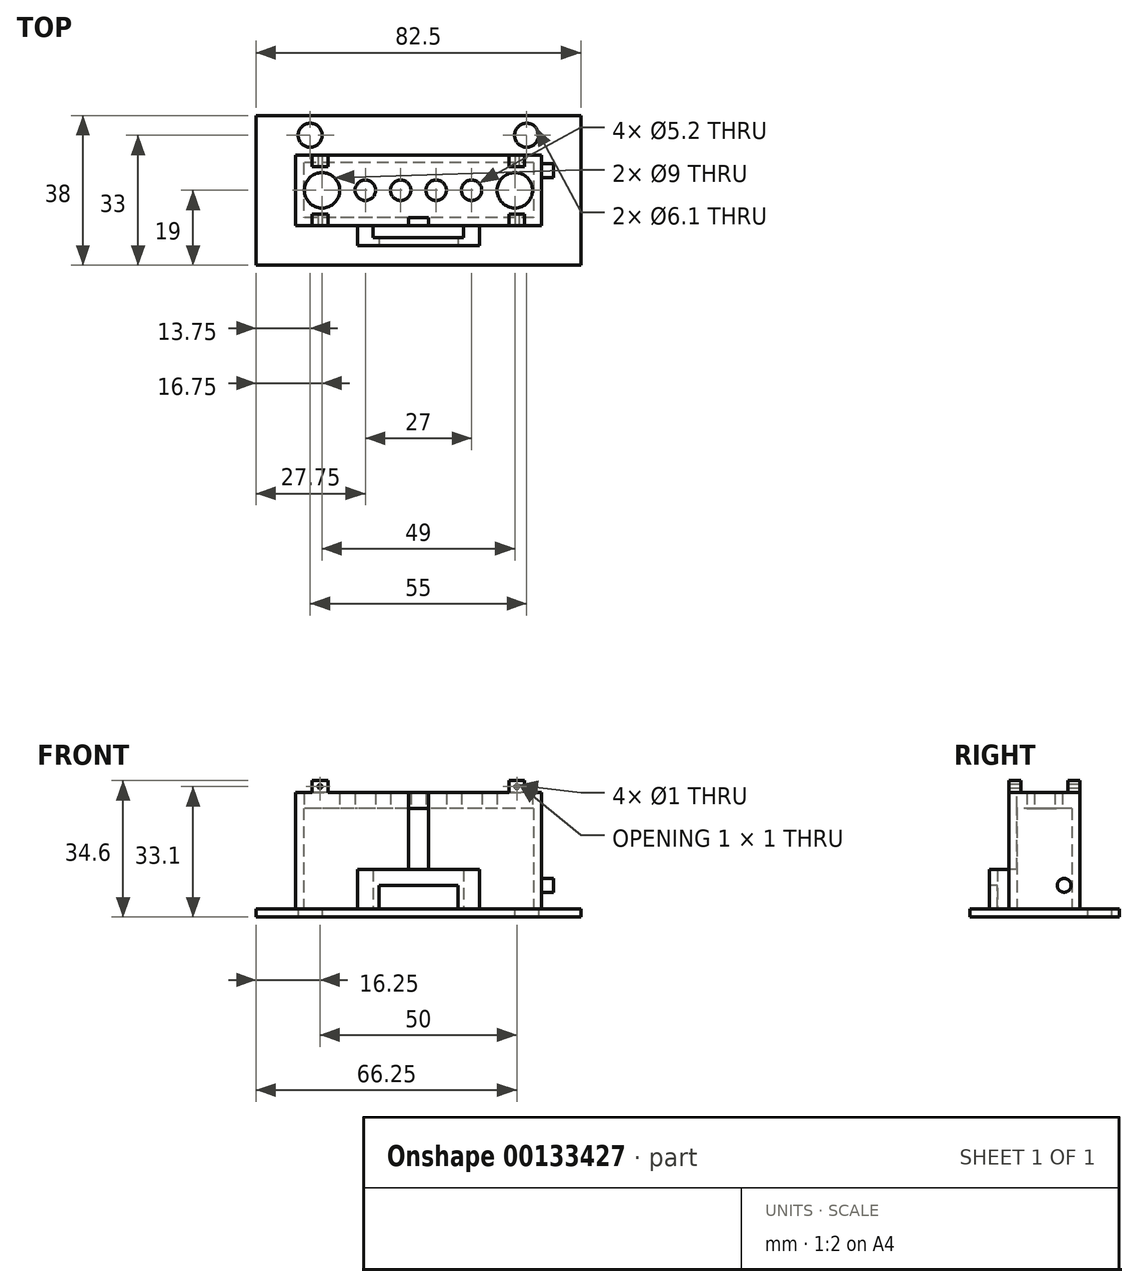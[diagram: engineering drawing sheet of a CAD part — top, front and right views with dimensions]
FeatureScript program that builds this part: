
annotation { "Feature Type Name" : "Feature", "Feature Type Description" : "" }
export const myFeature = defineFeature(function(context is Context, id is Id, definition is map)
    precondition{}
    {
        {
            var Q0;
            Q0=qCreatedBy(makeId("Top.planeOp"),FACE);
            var sketch = newSketch(context, id + "F0", { "sketchPlane" : qUnion([Q0])});
            skLineSegment(sketch, "E0.bottom", {"start": v(31.25, 9) * mm, "end": v(-31.25, 9) * mm});
            skLineSegment(sketch, "E0.top", {"start": v(31.25, -9) * mm, "end": v(-31.25, -9) * mm});
            skLineSegment(sketch, "E0.left", {"start": v(31.25, 9) * mm, "end": v(31.25, -9) * mm});
            skLineSegment(sketch, "E0.right", {"start": v(-31.25, 9) * mm, "end": v(-31.25, -9) * mm});
            skPoint(sketch, "E0.middle", {"position": v(0, 0) * mm});
            skLineSegment(sketch, "E1", {"start": v(-31.25, -9) * mm, "end": v(-31.25, 0) * mm});
            skLineSegment(sketch, "E2", {"start": v(-31.25, 0) * mm, "end": v(31.25, 0) * mm});
            skLineSegment(sketch, "E3", {"start": v(-13.5, 0) * mm, "end": v(-4.5, 0) * mm, "construction": true});
            skCircle(sketch, "E4", {"center": v(-4.5, 0) * mm, "radius": 2.6 * mm});
            skCircle(sketch, "E5.MirrorC", {"center": v(4.5, 0) * mm, "radius": 2.6 * mm});
            skLineSegment(sketch, "E6.0", {"start": v(29.25, -7) * mm, "end": v(-29.25, -7) * mm});
            skLineSegment(sketch, "E6.1", {"start": v(29.25, 7) * mm, "end": v(29.25, -7) * mm});
            skLineSegment(sketch, "E6.2", {"start": v(29.25, 7) * mm, "end": v(-29.25, 7) * mm});
            skLineSegment(sketch, "E6.3", {"start": v(-29.25, 7) * mm, "end": v(-29.25, -7) * mm});
            skCircle(sketch, "E7", {"center": v(-13.5, 0) * mm, "radius": 2.6 * mm});
            skLineSegment(sketch, "E8", {"start": v(4.5, 0) * mm, "end": v(4.5, 0) * mm});
            skCircle(sketch, "E9.MirrorC", {"center": v(13.5, 0) * mm, "radius": 2.6 * mm});
            skLineSegment(sketch, "E10.0", {"start": v(41.25, 19) * mm, "end": v(-41.25, 19) * mm});
            skLineSegment(sketch, "E10.1", {"start": v(41.25, 19) * mm, "end": v(41.25, -19) * mm});
            skLineSegment(sketch, "E10.2", {"start": v(41.25, -19) * mm, "end": v(-41.25, -19) * mm});
            skLineSegment(sketch, "E10.3", {"start": v(-41.25, 19) * mm, "end": v(-41.25, -19) * mm});
            skLineSegment(sketch, "E11", {"start": v(-41.25, 19) * mm, "end": v(-41.25, 14) * mm});
            skLineSegment(sketch, "E12", {"start": v(-41.25, 14) * mm, "end": v(-36.25, 14) * mm});
            skLineSegment(sketch, "E13", {"start": v(-13.5, 0) * mm, "end": v(-36.25, 0) * mm});
            skLineSegment(sketch, "E14", {"start": v(-36.25, 0) * mm, "end": v(-36.25, 14) * mm});
            skCircle(sketch, "E15.MirrorC", {"center": v(27.5, 14) * mm, "radius": 3.05 * mm});
            skCircle(sketch, "E16.MirrorC", {"center": v(-27.5, 14) * mm, "radius": 3.05 * mm});
            skLineSegment(sketch, "E17", {"start": v(0, 0) * mm, "end": v(24.5, 0) * mm});
            skCircle(sketch, "E18", {"center": v(24.5, 0) * mm, "radius": 4.5 * mm});
            skCircle(sketch, "E19.MirrorC", {"center": v(-24.5, 0) * mm, "radius": 4.5 * mm});
            skSolve(sketch);
        }
        {
            var Q0;
            {var subQ8=sQuery(id+"F0.wireOp",EDGE,"E0.top");Q0=makeQuery(id+"F0.imprint","IMPRINT",FACE,{"disambiguationData":[TD([[makeQuery(id+"F0.imprint","IMPRINT",EDGE,{"derivedFrom":subQ8}),-1.0]])]});}
            var Q1;
            {var subQ6=sQuery(id+"F0.wireOp",EDGE,"E0.bottom");Q1=makeQuery(id+"F0.imprint","IMPRINT",FACE,{"disambiguationData":[TD([[makeQuery(id+"F0.imprint","IMPRINT",EDGE,{"derivedFrom":subQ6}),1.0]])]});}
            extrude(context, id + "F1", {"entities" : qUnion([Q0, Q1]), "depth" : 31.6 * mm});
        }
        {
            var Q0;
            {var subQ8=sQuery(id+"F0.wireOp",EDGE,"E6.2");Q0=makeQuery(id+"F0.imprint","IMPRINT",FACE,{"disambiguationData":[TD([[makeQuery(id+"F0.imprint","IMPRINT",EDGE,{"derivedFrom":subQ8}),1.0]])]});}
            var Q1;
            {var subQ0=sQuery(id+"F0.wireOp",EDGE,"E6.0");Q1=makeQuery(id+"F0.imprint","IMPRINT",FACE,{"disambiguationData":[TD([[makeQuery(id+"F0.imprint","IMPRINT",EDGE,{"derivedFrom":subQ0}),-1.0]])]});}
            extrude(context, id + "F2", {"entities" : qUnion([Q0, Q1]), "operationType" : NewBodyOperationType.ADD, "depth" : 31.6 * mm, "hasSecondDirection" : true, "secondDirectionOppositeDirection" : false, "secondDirectionDepth" : 27.6 * mm});
        }
        {
            var Q0;
            {var subQ0=sQuery(id+"F0.wireOp",EDGE,"E0.bottom");Q0=makeQuery(id+"F0.imprint","IMPRINT",FACE,{"disambiguationData":[TD([[makeQuery(id+"F0.imprint","IMPRINT",EDGE,{"derivedFrom":subQ0}),-1.0]])]});}
            extrude(context, id + "F3", {"entities" : qUnion([Q0]), "operationType" : NewBodyOperationType.ADD, "depth" : 2 * mm});
        }
        {
            var Q0;
            Q0=makeQuery(id+"F1.opExtrude","SWEPT_FACE",FACE,{"disambiguationData":[OSD([sQuery(id+"F0.wireOp",EDGE,"E0.top")])]});
            var sketch = newSketch(context, id + "F4", { "sketchPlane" : qUnion([Q0])});
            skLineSegment(sketch, "E20", {"start": v(0, 2) * mm, "end": v(0, 31.6) * mm});
            skLineSegment(sketch, "E21.bottom", {"start": v(2.5, 31.6) * mm, "end": v(-2.5, 31.6) * mm});
            skPoint(sketch, "E21.middle", {"position": v(0, 16.8) * mm});
            skLineSegment(sketch, "E22", {"start": v(9, 2) * mm, "end": v(18, 2) * mm});
            skLineSegment(sketch, "E23", {"start": v(-9, 2) * mm, "end": v(-18, 2) * mm});
            skLineSegment(sketch, "E24.bottom", {"start": v(-15.5, 31.6) * mm, "end": v(-20.5, 31.6) * mm});
            skLineSegment(sketch, "E24.top", {"start": v(-15.5, 2) * mm, "end": v(-20.5, 2) * mm});
            skPoint(sketch, "E24.middle", {"position": v(-18, 16.8) * mm});
            skLineSegment(sketch, "E25.bottom", {"start": v(-6.5, 31.6) * mm, "end": v(-11.5, 31.6) * mm});
            skLineSegment(sketch, "E25.top", {"start": v(-6.5, 2) * mm, "end": v(-11.5, 2) * mm});
            skPoint(sketch, "E25.middle", {"position": v(-9, 16.8) * mm});
            skLineSegment(sketch, "E26.bottom", {"start": v(11.5, 31.6) * mm, "end": v(6.5, 31.6) * mm});
            skLineSegment(sketch, "E26.top", {"start": v(11.5, 2) * mm, "end": v(6.5, 2) * mm});
            skPoint(sketch, "E26.middle", {"position": v(9, 16.8) * mm});
            skLineSegment(sketch, "E27.bottom", {"start": v(20.5, 31.6) * mm, "end": v(15.5, 31.6) * mm});
            skLineSegment(sketch, "E27.top", {"start": v(20.5, 2) * mm, "end": v(15.5, 2) * mm});
            skPoint(sketch, "E27.middle", {"position": v(18, 16.8) * mm});
            skLineSegment(sketch, "E28", {"start": v(2.5, 12) * mm, "end": v(-2.5, 12) * mm});
            skLineSegment(sketch, "E29", {"start": v(2.5, 12) * mm, "end": v(2.5, 31.6) * mm});
            skLineSegment(sketch, "E30", {"start": v(-2.5, 12) * mm, "end": v(-2.5, 31.6) * mm});
            skSolve(sketch);
        }
        {
            var Q0;
            {var subQ0=sQuery(id+"F4.wireOp",EDGE,"E20");Q0=makeQuery(id+"F4.imprint","IMPRINT",FACE,{"disambiguationData":[TD([[makeQuery(id+"F4.imprint","IMPRINT",EDGE,{"derivedFrom":subQ0}),1.0]])]});}
            var Q1;
            {var subQ0=sQuery(id+"F4.wireOp",EDGE,"E20");Q1=makeQuery(id+"F4.imprint","IMPRINT",FACE,{"disambiguationData":[TD([[makeQuery(id+"F4.imprint","IMPRINT",EDGE,{"derivedFrom":subQ0}),-1.0]])]});}
            var Q2;
            {var subQ0=sQuery(id+"F4.wireOp",EDGE,"mmB4Bz2B-6gc4-3Cgj-2VaW-CwXLaNoJo5JT");Q2=makeQuery(id+"F4.imprint","IMPRINT",FACE,{"disambiguationData":[TD([[makeQuery(id+"F4.imprint","IMPRINT",EDGE,{"derivedFrom":subQ0}),1.0]])]});}
            var Q3;
            {var subQ0=sQuery(id+"F4.wireOp",EDGE,"mmB4Bz2B-6gc4-3Cgj-2VaW-CwXLaNoJo5JT");Q3=makeQuery(id+"F4.imprint","IMPRINT",FACE,{"disambiguationData":[TD([[makeQuery(id+"F4.imprint","IMPRINT",EDGE,{"derivedFrom":subQ0}),-1.0]])]});}
            var Q4;
            {var subQ0=sQuery(id+"F4.wireOp",EDGE,"Rwbuybag-eQZT-opry-GWMa-gLoR60jAGtG4");Q4=makeQuery(id+"F4.imprint","IMPRINT",FACE,{"disambiguationData":[TD([[makeQuery(id+"F4.imprint","IMPRINT",EDGE,{"derivedFrom":subQ0}),1.0]])]});}
            var Q5;
            {var subQ0=sQuery(id+"F4.wireOp",EDGE,"Rwbuybag-eQZT-opry-GWMa-gLoR60jAGtG4");Q5=makeQuery(id+"F4.imprint","IMPRINT",FACE,{"disambiguationData":[TD([[makeQuery(id+"F4.imprint","IMPRINT",EDGE,{"derivedFrom":subQ0}),-1.0]])]});}
            var Q6;
            {var subQ0=sQuery(id+"F4.wireOp",EDGE,"ruHpWR7G-ukM4-UtCa-b8dm-bSCTeueY3kcp");Q6=makeQuery(id+"F4.imprint","IMPRINT",FACE,{"disambiguationData":[TD([[makeQuery(id+"F4.imprint","IMPRINT",EDGE,{"derivedFrom":subQ0}),-1.0]])]});}
            var Q7;
            {var subQ0=sQuery(id+"F4.wireOp",EDGE,"ruHpWR7G-ukM4-UtCa-b8dm-bSCTeueY3kcp");Q7=makeQuery(id+"F4.imprint","IMPRINT",FACE,{"disambiguationData":[TD([[makeQuery(id+"F4.imprint","IMPRINT",EDGE,{"derivedFrom":subQ0}),1.0]])]});}
            var Q8;
            {var subQ0=sQuery(id+"F4.wireOp",EDGE,"ibgEnuu2-NqSA-dH6u-1LKB-RHXitZY2cpsr");Q8=makeQuery(id+"F4.imprint","IMPRINT",FACE,{"disambiguationData":[TD([[makeQuery(id+"F4.imprint","IMPRINT",EDGE,{"derivedFrom":subQ0}),1.0]])]});}
            var Q9;
            {var subQ0=sQuery(id+"F4.wireOp",EDGE,"ibgEnuu2-NqSA-dH6u-1LKB-RHXitZY2cpsr");Q9=makeQuery(id+"F4.imprint","IMPRINT",FACE,{"disambiguationData":[TD([[makeQuery(id+"F4.imprint","IMPRINT",EDGE,{"derivedFrom":subQ0}),-1.0]])]});}
            extrude(context, id + "F5", {"entities" : qUnion([Q0, Q1, Q2, Q3, Q4, Q5, Q6, Q7, Q8, Q9]), "operationType" : NewBodyOperationType.REMOVE, "oppositeDirection" : true, "depth" : 2 * mm});
        }
        {
            var Q0;
            {var subQ0=sQuery(id+"F0.wireOp",EDGE,"E6.3");var subQ1=sQuery(id+"F0.wireOp",EDGE,"E6.2");var subQ2=sQuery(id+"F0.wireOp",EDGE,"E6.1");var subQ3=sQuery(id+"F0.wireOp",EDGE,"E6.0");Q0=makeQuery(id+"F2.boolean.opBoolean","MERGE",FACE,{"derivedFrom":[makeQuery(id+"F1.opExtrude","CAP_FACE",FACE,{"disambiguationData":[OSD([sQuery(id+"F0.wireOp",EDGE,"E0.bottom"),sQuery(id+"F0.wireOp",EDGE,"E0.top"),sQuery(id+"F0.wireOp",EDGE,"E0.left"),sQuery(id+"F0.wireOp",EDGE,"E0.right"),sQuery(id+"F0.wireOp",EDGE,"E1"),subQ3,subQ2,subQ1,subQ0])],"isStart":false}),makeQuery(id+"F2.opExtrude","CAP_FACE",FACE,{"disambiguationData":[OSD([sQuery(id+"F0.wireOp",EDGE,"E4"),sQuery(id+"F0.wireOp",EDGE,"E5.MirrorC"),subQ3,subQ2,subQ1,subQ0,sQuery(id+"F0.wireOp",EDGE,"E7"),sQuery(id+"F0.wireOp",EDGE,"E9.MirrorC"),sQuery(id+"F0.wireOp",EDGE,"E18"),sQuery(id+"F0.wireOp",EDGE,"E19.MirrorC")])],"isStart":false})]});}
            var sketch = newSketch(context, id + "F6", { "sketchPlane" : qUnion([Q0])});
            skLineSegment(sketch, "E31", {"start": v(-31.25, -9) * mm, "end": v(-29, -9) * mm});
            skLineSegment(sketch, "E32", {"start": v(-29, -9) * mm, "end": v(-25, -9) * mm});
            skLineSegment(sketch, "E33", {"start": v(-25, -9) * mm, "end": v(-27, -9) * mm});
            skLineSegment(sketch, "E34", {"start": v(-25, -9) * mm, "end": v(-23, -9) * mm});
            skLineSegment(sketch, "E35", {"start": v(-23, -9) * mm, "end": v(-23, -6) * mm});
            skLineSegment(sketch, "E36", {"start": v(-23, -6) * mm, "end": v(-25, -6) * mm});
            skLineSegment(sketch, "E37", {"start": v(-25, -6) * mm, "end": v(-27, -6) * mm});
            skLineSegment(sketch, "E38", {"start": v(-27, -6) * mm, "end": v(-27, -9) * mm});
            skLineSegment(sketch, "E39.MirrorCS", {"start": v(23, -9) * mm, "end": v(23, -6) * mm});
            skLineSegment(sketch, "E40.MirrorCS", {"start": v(23, -6) * mm, "end": v(25, -6) * mm});
            skLineSegment(sketch, "E41.MirrorCS", {"start": v(25, -6) * mm, "end": v(27, -6) * mm});
            skLineSegment(sketch, "E42.MirrorCS", {"start": v(27, -6) * mm, "end": v(27, -9) * mm});
            skLineSegment(sketch, "E43.MirrorCS", {"start": v(25, -9) * mm, "end": v(27, -9) * mm});
            skLineSegment(sketch, "E44.MirrorCS", {"start": v(25, -9) * mm, "end": v(23, -9) * mm});
            skLineSegment(sketch, "E45.MirrorCS", {"start": v(-23, 9) * mm, "end": v(-23, 6) * mm});
            skLineSegment(sketch, "E46.MirrorCS", {"start": v(-23, 6) * mm, "end": v(-25, 6) * mm});
            skLineSegment(sketch, "E47.MirrorCS", {"start": v(-25, 6) * mm, "end": v(-27, 6) * mm});
            skLineSegment(sketch, "E48.MirrorCS", {"start": v(-27, 6) * mm, "end": v(-27, 9) * mm});
            skLineSegment(sketch, "E49.MirrorCS", {"start": v(-25, 9) * mm, "end": v(-27, 9) * mm});
            skLineSegment(sketch, "E50.MirrorCS", {"start": v(-25, 9) * mm, "end": v(-23, 9) * mm});
            skLineSegment(sketch, "E51.MirrorCS", {"start": v(27, 6) * mm, "end": v(27, 9) * mm});
            skLineSegment(sketch, "E52.MirrorCS", {"start": v(25, 6) * mm, "end": v(27, 6) * mm});
            skLineSegment(sketch, "E53.MirrorCS", {"start": v(23, 6) * mm, "end": v(25, 6) * mm});
            skLineSegment(sketch, "E54.MirrorCS", {"start": v(23, 9) * mm, "end": v(23, 6) * mm});
            skLineSegment(sketch, "E55.MirrorCS", {"start": v(25, 9) * mm, "end": v(23, 9) * mm});
            skLineSegment(sketch, "E56.MirrorCS", {"start": v(25, 9) * mm, "end": v(27, 9) * mm});
            skSolve(sketch);
        }
        {
            var Q0;
            Q0=qSketchRegion(id+"F6",true);
            extrude(context, id + "F7", {"entities" : qUnion([Q0]), "operationType" : NewBodyOperationType.ADD, "depth" : 3 * mm});
        }
        {
            var Q0;
            {var subQ7=sQuery(id+"F0.wireOp",EDGE,"E0.top");Q0=makeQuery(id+"F7.boolean.opBoolean","MERGE",FACE,{"derivedFrom":[makeQuery(id+"F5.boolean.opBoolean","SPLIT",FACE,{"disambiguationData":[TD([makeQuery(id+"F5.opExtrude","SWEPT_FACE",FACE,{"disambiguationData":[OSD([sQuery(id+"F4.wireOp",EDGE,"E24.right")])]})])],"derivedFrom":makeQuery(id+"F1.opExtrude","SWEPT_FACE",FACE,{"disambiguationData":[OSD([subQ7])]})}),makeQuery(id+"F7.opExtrude","SWEPT_FACE",FACE,{"disambiguationData":[OSD([sQuery(id+"F6.wireOp",EDGE,"E33"),sQuery(id+"F6.wireOp",EDGE,"E34")])]})]});}
            var sketch = newSketch(context, id + "F8", { "sketchPlane" : qUnion([Q0])});
            skLineSegment(sketch, "E57", {"start": v(-27, 34.6) * mm, "end": v(-25, 34.6) * mm});
            skLineSegment(sketch, "E58", {"start": v(-25, 34.6) * mm, "end": v(-25, 33.1) * mm});
            skCircle(sketch, "E59", {"center": v(-25, 33.1) * mm, "radius": 0.5 * mm});
            skCircle(sketch, "E60.MirrorC", {"center": v(25, 33.1) * mm, "radius": 0.5 * mm});
            skSolve(sketch);
        }
        {
            var Q0;
            Q0=qSketchRegion(id+"F8",true);
            extrude(context, id + "F9", {"entities" : qUnion([Q0]), "operationType" : NewBodyOperationType.REMOVE, "oppositeDirection" : true, "depth" : 25 * mm});
        }
        {
            var Q0;
            Q0=makeQuery(id+"F1.opExtrude","SWEPT_FACE",FACE,{"disambiguationData":[OSD([sQuery(id+"F0.wireOp",EDGE,"E0.left")])]});
            var sketch = newSketch(context, id + "F10", { "sketchPlane" : qUnion([Q0])});
            skLineSegment(sketch, "E61", {"start": v(9, 2) * mm, "end": v(9, 8) * mm});
            skLineSegment(sketch, "E62", {"start": v(9, 8) * mm, "end": v(5, 8) * mm});
            skCircle(sketch, "E63", {"center": v(5, 8) * mm, "radius": 1.75 * mm});
            skSolve(sketch);
        }
        {
            var Q0;
            Q0 = qSketchRegion(id + "F10", true);
            extrude(context, id + "F11", {"entities" : qUnion([Q0]), "operationType" : NewBodyOperationType.ADD, "depth" : 3 * mm});
        }
        {
            var Q0;
            Q0=makeQuery(id+"F5.boolean.opBoolean","MERGE",FACE,{"derivedFrom":[makeQuery(id+"F3.opExtrude","CAP_FACE",FACE,{"disambiguationData":[OSD([sQuery(id+"F0.wireOp",EDGE,"E0.bottom"),sQuery(id+"F0.wireOp",EDGE,"E0.top"),sQuery(id+"F0.wireOp",EDGE,"E0.left"),sQuery(id+"F0.wireOp",EDGE,"E0.right"),sQuery(id+"F0.wireOp",EDGE,"E1"),sQuery(id+"F0.wireOp",EDGE,"E10.0"),sQuery(id+"F0.wireOp",EDGE,"E10.1"),sQuery(id+"F0.wireOp",EDGE,"E10.2"),sQuery(id+"F0.wireOp",EDGE,"E10.3"),sQuery(id+"F0.wireOp",EDGE,"E11"),sQuery(id+"F0.wireOp",EDGE,"E15.MirrorC"),sQuery(id+"F0.wireOp",EDGE,"E16.MirrorC")])],"isStart":false}),makeQuery(id+"F5.opExtrude","SWEPT_FACE",FACE,{"disambiguationData":[OSD([sQuery(id+"F4.wireOp",EDGE,"kKXx591k-0a11-7VBp-Juem-MAlILkcbwSke"),sQuery(id+"F4.wireOp",EDGE,"DCKLYDHC-zZUY-w4WA-nGlo-Jf28eUDDzCgn")])]}),makeQuery(id+"F5.opExtrude","SWEPT_FACE",FACE,{"disambiguationData":[OSD([sQuery(id+"F4.wireOp",EDGE,"E24.top")])]}),makeQuery(id+"F5.opExtrude","SWEPT_FACE",FACE,{"disambiguationData":[OSD([sQuery(id+"F4.wireOp",EDGE,"E25.top")])]}),makeQuery(id+"F5.opExtrude","SWEPT_FACE",FACE,{"disambiguationData":[OSD([sQuery(id+"F4.wireOp",EDGE,"E26.top")])]}),makeQuery(id+"F5.opExtrude","SWEPT_FACE",FACE,{"disambiguationData":[OSD([sQuery(id+"F4.wireOp",EDGE,"E27.top")])]})]});
            var sketch = newSketch(context, id + "F12", { "sketchPlane" : qUnion([Q0])});
            skLineSegment(sketch, "E64", {"start": v(-31.25, -9) * mm, "end": v(0, -9) * mm});
            skLineSegment(sketch, "E65", {"start": v(0, -9) * mm, "end": v(0, -12) * mm});
            skLineSegment(sketch, "E66", {"start": v(15.5, -11) * mm, "end": v(15.5, -14) * mm});
            skLineSegment(sketch, "E67", {"start": v(15.5, -14) * mm, "end": v(0, -14) * mm});
            skLineSegment(sketch, "E68.MirrorCS", {"start": v(-15.5, -11) * mm, "end": v(-15.5, -14) * mm});
            skLineSegment(sketch, "E69.MirrorCS", {"start": v(-15.5, -14) * mm, "end": v(0, -14) * mm});
            skLineSegment(sketch, "E70", {"start": v(15.5, -11) * mm, "end": v(15.5, -9) * mm});
            skLineSegment(sketch, "E71", {"start": v(15.5, -9) * mm, "end": v(11.5, -9) * mm});
            skLineSegment(sketch, "E72", {"start": v(11.5, -9) * mm, "end": v(11.5, -12) * mm});
            skLineSegment(sketch, "E73", {"start": v(11.5, -12) * mm, "end": v(0, -12) * mm});
            skLineSegment(sketch, "E74.MirrorCS", {"start": v(-11.5, -9) * mm, "end": v(-11.5, -12) * mm});
            skLineSegment(sketch, "E75.MirrorCS", {"start": v(-15.5, -9) * mm, "end": v(-11.5, -9) * mm});
            skLineSegment(sketch, "E76.MirrorCS", {"start": v(-15.5, -11) * mm, "end": v(-15.5, -9) * mm});
            skLineSegment(sketch, "E77.MirrorCS", {"start": v(-11.5, -12) * mm, "end": v(0, -12) * mm});
            skSolve(sketch);
        }
        {
            var Q0;
            Q0=makeQuery(id+"F12.imprint","IMPRINT",FACE,{"disambiguationData":[TD([[makeQuery(id+"F12.imprint","IMPRINT",EDGE,{"derivedFrom":sQuery(id+"F12.wireOp",EDGE,"E66")}),-1.0]])]});
            extrude(context, id + "F13", {"entities" : qUnion([Q0]), "operationType" : NewBodyOperationType.ADD, "depth" : 10 * mm});
        }
        {
            var Q0;
            Q0=makeQuery(id+"F13.opExtrude","SWEPT_FACE",FACE,{"disambiguationData":[OSD([sQuery(id+"F12.wireOp",EDGE,"E67"),sQuery(id+"F12.wireOp",EDGE,"E69.MirrorCS")])]});
            var sketch = newSketch(context, id + "F14", { "sketchPlane" : qUnion([Q0])});
            skLineSegment(sketch, "E78", {"start": v(0, 2) * mm, "end": v(10, 2) * mm});
            skLineSegment(sketch, "E79", {"start": v(10, 2) * mm, "end": v(10, 8) * mm});
            skLineSegment(sketch, "E80", {"start": v(10, 8) * mm, "end": v(0, 8) * mm});
            skLineSegment(sketch, "E81.MirrorCS", {"start": v(-10, 8) * mm, "end": v(0, 8) * mm});
            skLineSegment(sketch, "E82.MirrorCS", {"start": v(-10, 2) * mm, "end": v(-10, 8) * mm});
            skSolve(sketch);
        }
        {
            var Q0;
            Q0 = qSketchRegion(id + "F14", true);
            var Q1;
            {var subQ0=sQuery(id+"F14.wireOp",EDGE,"E78");Q1=makeQuery(id+"F14.imprint","IMPRINT",FACE,{"disambiguationData":[TD([[makeQuery(id+"F14.imprint","IMPRINT",EDGE,{"derivedFrom":subQ0}),1.0]])]});}
            extrude(context, id + "F15", {"entities" : qUnion([Q0, Q1]), "operationType" : NewBodyOperationType.REMOVE, "oppositeDirection" : true, "depth" : 4 * mm});
        }
    });
